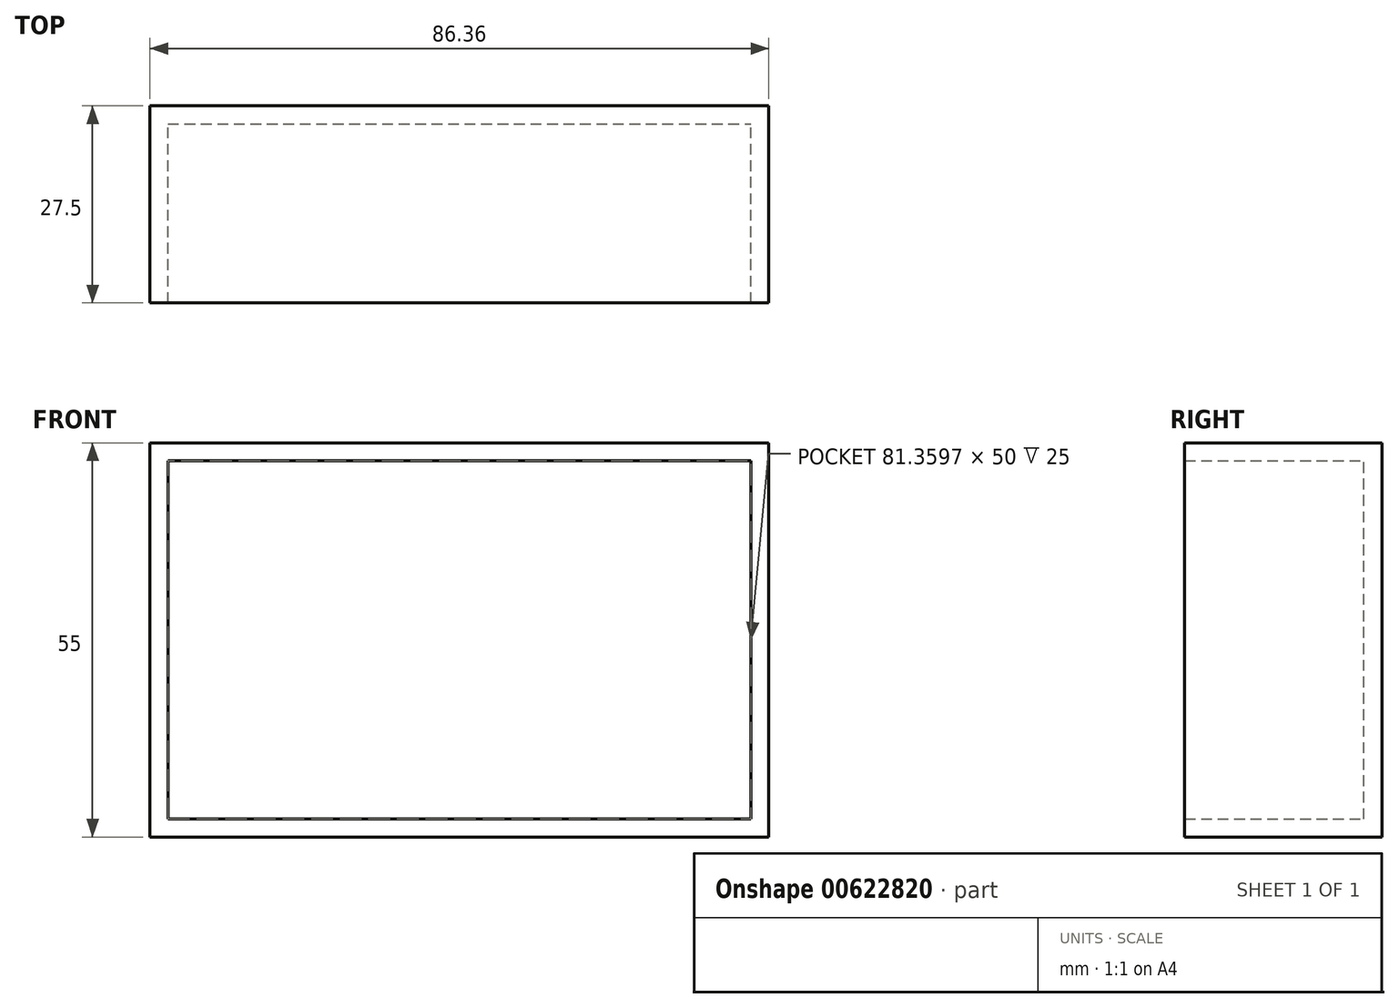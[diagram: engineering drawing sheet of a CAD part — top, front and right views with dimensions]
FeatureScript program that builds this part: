
annotation { "Feature Type Name" : "Feature", "Feature Type Description" : "" }
export const myFeature = defineFeature(function(context is Context, id is Id, definition is map)
    precondition{}
    {
        {
            var Q0;
            Q0=qCreatedBy(makeId("Front.planeOp"),FACE);
            var sketch = newSketch(context, id + "F0", { "sketchPlane" : qUnion([Q0])});
            skLineSegment(sketch, "E0.bottom", {"start": v(0, 0) * mm, "end": v(81.36, 0) * mm});
            skLineSegment(sketch, "E0.top", {"start": v(0, 50) * mm, "end": v(81.36, 50) * mm});
            skLineSegment(sketch, "E0.left", {"start": v(0, 0) * mm, "end": v(0, 50) * mm});
            skLineSegment(sketch, "E0.right", {"start": v(81.36, 0) * mm, "end": v(81.36, 50) * mm});
            skSolve(sketch);
        }
        {
            var Q0;
            Q0 = qSketchRegion(id + "F0", true);
            extrude(context, id + "F1", {"entities" : qUnion([Q0]), "depth" : 25 * mm, "offsetDistance" : 25 * mm});
        }
        {
            var Q0;
            Q0=makeQuery(id+"F1.opExtrude","CAP_FACE",FACE,{"disambiguationData":[OSD([sQuery(id+"F0.wireOp",EDGE,"E0.bottom"),sQuery(id+"F0.wireOp",EDGE,"E0.top"),sQuery(id+"F0.wireOp",EDGE,"E0.left"),sQuery(id+"F0.wireOp",EDGE,"E0.right")])],"isStart":false});
            shell(context, id + "F2", {"entities" : qUnion([Q0]), "thickness" : 2.5 * mm, "oppositeDirection" : true});
        }
    });
